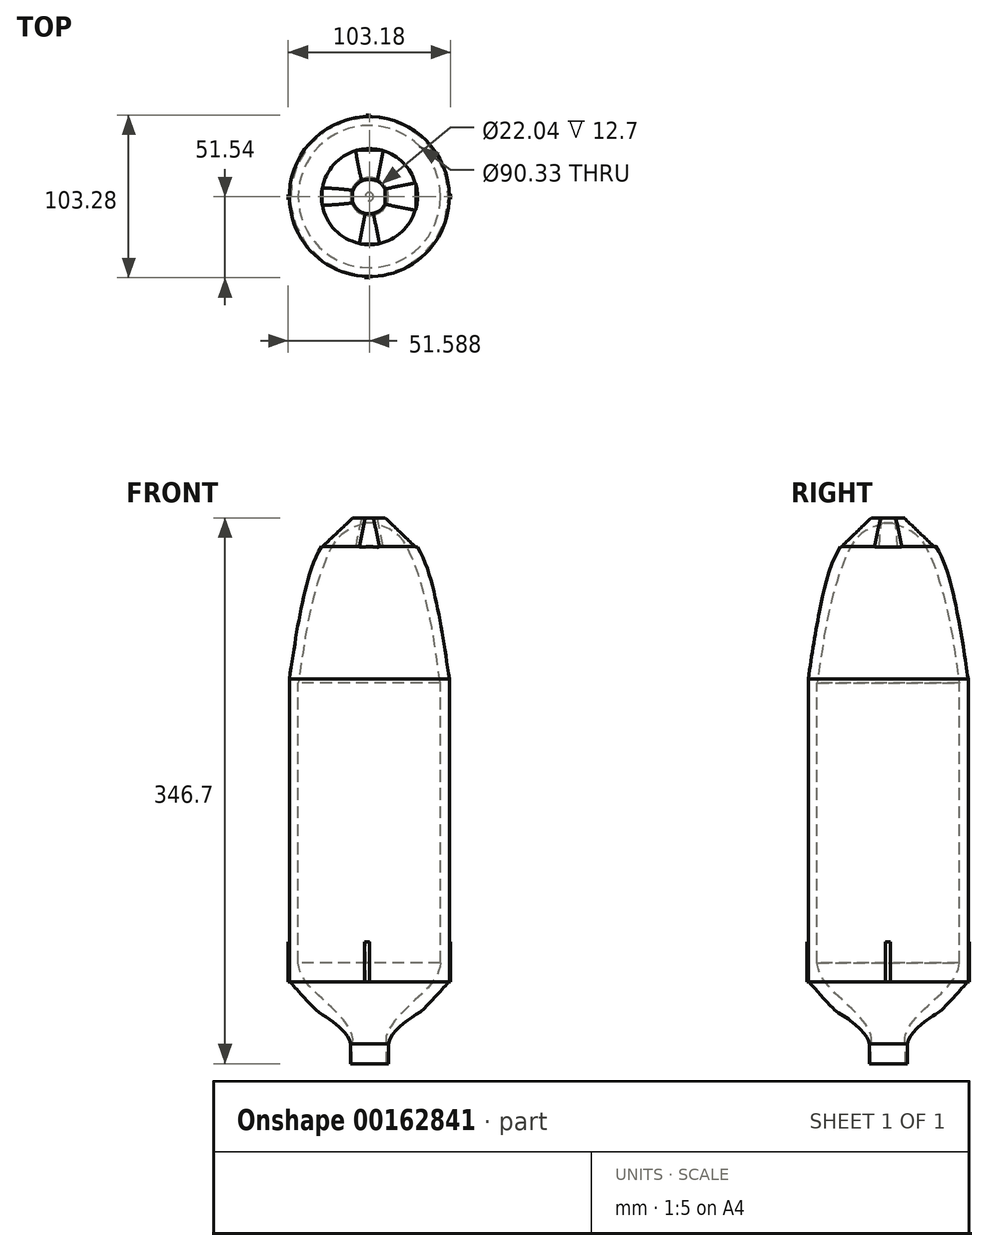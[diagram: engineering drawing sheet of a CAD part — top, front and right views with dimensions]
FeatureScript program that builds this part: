
annotation { "Feature Type Name" : "Feature", "Feature Type Description" : "" }
export const myFeature = defineFeature(function(context is Context, id is Id, definition is map)
    precondition{}
    {
        {
            var Q0;
            Q0=qCreatedBy(makeId("Front.planeOp"),FACE);
            var sketch = newSketch(context, id + "F0", { "sketchPlane" : qUnion([Q0])});
            skLineSegment(sketch, "E0", {"start": v(-60.21, 31.3) * mm, "end": v(-60.21, -146.5) * mm});
            skLineSegment(sketch, "E1", {"start": v(-9.41, 186.57) * mm, "end": v(-9.41, -181.27) * mm});
            skLineSegment(sketch, "E2", {"start": v(-60.21, 31.3) * mm, "end": v(-60.21, 133.73) * mm});
            skFitSpline(sketch, "E3", {"points": [v(-60.21, 31.3) * mm, v(-53.46, 72.41) * mm, v(-39.78, 115.49) * mm, v(-20.52, 133.73) * mm], "startDerivative": vector(16.73, 112.62) * mm, "endDerivative": vector(74.74, 52.6) * mm});
            skLineSegment(sketch, "E4", {"start": v(-20.52, 133.73) * mm, "end": v(-9.41, 133.73) * mm});
            skLineSegment(sketch, "E5", {"start": v(-21.48, -200.27) * mm, "end": v(-9.22, -200.27) * mm});
            skLineSegment(sketch, "E6", {"start": v(-54.58, 28.83) * mm, "end": v(-54.58, -148.97) * mm});
            skLineSegment(sketch, "E7", {"start": v(-3.78, 184.45) * mm, "end": v(-3.78, -183.39) * mm});
            skFitSpline(sketch, "E8", {"points": [v(-54.58, 28.83) * mm, v(-48.05, 69.53) * mm, v(-34.17, 113.63) * mm, v(-12.02, 130.37) * mm], "startDerivative": vector(18.83, 112.22) * mm, "endDerivative": vector(142.02, 42.2) * mm});
            skLineSegment(sketch, "E9", {"start": v(-12.02, 130.37) * mm, "end": v(-3.78, 130.37) * mm});
            skFitSpline(sketch, "E10", {"points": [v(-54.58, -148.97) * mm, v(-46.32, -164.98) * mm, v(-28.75, -182.02) * mm, v(-20.43, -200.27) * mm], "startDerivative": vector(6.77, -62.42) * mm, "endDerivative": vector(-19.43, -49.45) * mm});
            skLineSegment(sketch, "E11", {"start": v(-20.43, -200.27) * mm, "end": v(93.11, -200.27) * mm});
            skLineSegment(sketch, "E12", {"start": v(-60.21, -146.5) * mm, "end": v(-60.21, -161.1) * mm});
            skLineSegment(sketch, "E13", {"start": v(-60.21, -161.1) * mm, "end": v(-59.64, -161.1) * mm});
            skFitSpline(sketch, "E14", {"points": [v(-59.64, -161.1) * mm, v(-54.8, -166.59) * mm, v(-43.08, -179) * mm, v(-36.44, -183.52) * mm, v(-21.48, -200.27) * mm], "startDerivative": vector(23.82, -31.92) * mm, "endDerivative": vector(1.05, -49.25) * mm});
            skLineSegment(sketch, "E15", {"start": v(-39.78, 115.49) * mm, "end": v(-20.52, 133.73) * mm});
            skSolve(sketch);
        }
        {
            var Q0;
            Q0=makeQuery(id+"F0.imprint","IMPRINT",FACE,{"disambiguationData":[TD([[makeQuery(id+"F0.imprint","IMPRINT",EDGE,{"derivedFrom":sQuery(id+"F0.wireOp",EDGE,"E0")}),1.0]])]});
            var Q1;
            Q1=sQuery(id+"F0.wireOp",EDGE,"E1");
            revolve(context, id + "F1", {"entities" : qUnion([Q0]), "axis" : qUnion([Q1]), "revolveType" : RevolveType.FULL});
        }
        {
            var Q0;
            Q0=makeQuery(id+"F1.opRevolve","SWEPT_FACE",FACE,{"disambiguationData":[OSD([sQuery(id+"F0.wireOp",EDGE,"E13")])]});
            var sketch = newSketch(context, id + "F2", { "sketchPlane" : qUnion([Q0])});
            skLineSegment(sketch, "E16.bottom", {"start": v(-61, 2) * mm, "end": v(-60.2, 2) * mm});
            skLineSegment(sketch, "E16.top", {"start": v(-61, -1.35) * mm, "end": v(-60.2, -1.35) * mm});
            skLineSegment(sketch, "E16.left", {"start": v(-61, 2) * mm, "end": v(-61, -1.35) * mm});
            skLineSegment(sketch, "E16.right", {"start": v(-60.2, 2) * mm, "end": v(-60.2, -1.35) * mm});
            skLineSegment(sketch, "E17.bottom", {"start": v(-12.36, 50.8) * mm, "end": v(-9.4, 50.8) * mm});
            skLineSegment(sketch, "E17.top", {"start": v(-12.36, 50.23) * mm, "end": v(-9.4, 50.23) * mm});
            skLineSegment(sketch, "E17.left", {"start": v(-12.36, 50.8) * mm, "end": v(-12.36, 50.23) * mm});
            skLineSegment(sketch, "E17.right", {"start": v(-9.4, 50.8) * mm, "end": v(-9.4, 50.23) * mm});
            skLineSegment(sketch, "E18.bottom", {"start": v(42.18, 1.62) * mm, "end": v(40.8, 1.62) * mm});
            skLineSegment(sketch, "E18.top", {"start": v(42.18, -1.51) * mm, "end": v(40.8, -1.51) * mm});
            skLineSegment(sketch, "E18.left", {"start": v(42.18, 1.62) * mm, "end": v(42.18, -1.51) * mm});
            skLineSegment(sketch, "E18.right", {"start": v(40.8, 1.62) * mm, "end": v(40.8, -1.51) * mm});
            skLineSegment(sketch, "E19.bottom", {"start": v(-11.37, -50.2) * mm, "end": v(-8.54, -50.2) * mm});
            skLineSegment(sketch, "E19.top", {"start": v(-11.37, -51.74) * mm, "end": v(-8.54, -51.74) * mm});
            skLineSegment(sketch, "E19.left", {"start": v(-11.37, -50.2) * mm, "end": v(-11.37, -51.74) * mm});
            skLineSegment(sketch, "E19.right", {"start": v(-8.54, -50.2) * mm, "end": v(-8.54, -51.74) * mm});
            skLineSegment(sketch, "E20.bottom", {"start": v(-60.2, 2) * mm, "end": v(-59.62, 2) * mm});
            skLineSegment(sketch, "E20.top", {"start": v(-60.2, -1.36) * mm, "end": v(-59.62, -1.36) * mm});
            skLineSegment(sketch, "E20.left", {"start": v(-60.2, 2) * mm, "end": v(-60.2, -1.36) * mm});
            skLineSegment(sketch, "E20.right", {"start": v(-59.62, 2) * mm, "end": v(-59.62, -1.36) * mm});
            skLineSegment(sketch, "E21.bottom", {"start": v(-12.36, 50.8) * mm, "end": v(-9.39, 50.8) * mm});
            skLineSegment(sketch, "E21.top", {"start": v(-12.36, 51.54) * mm, "end": v(-9.39, 51.54) * mm});
            skLineSegment(sketch, "E21.left", {"start": v(-12.36, 50.8) * mm, "end": v(-12.36, 51.54) * mm});
            skLineSegment(sketch, "E21.right", {"start": v(-9.39, 50.8) * mm, "end": v(-9.39, 51.54) * mm});
            skSolve(sketch);
        }
        {
            var Q0;
            {var subQ1=sQuery(id+"F0.wireOp",EDGE,"E13");var subQ4=makeQuery(id+"F1.opRevolve","SWEPT_EDGE",EDGE,{"disambiguationData":[OSD([sQuery(id+"F0.wireOp",EDGE,"E12"),subQ1])]});var subQ6=sQuery(id+"F2.wireOp",EDGE,"E19.right");var subQ8=makeQuery(id+"F2.imprint","INTERSECT",VERTEX,{"derivedFrom":[subQ4,subQ6]});Q0=makeQuery(id+"F2.imprint","IMPRINT",FACE,{"disambiguationData":[TD([[makeQuery(id+"F2.imprint","IMPRINT",EDGE,{"disambiguationData":[TD([[subQ8,1.0]])],"derivedFrom":subQ6}),-1.0]])]});}
            var Q1;
            {var subQ0=sQuery(id+"F2.wireOp",EDGE,"E18.bottom");var subQ6=sQuery(id+"F2.wireOp",EDGE,"E18.right");var subQ10=makeQuery(id+"F2.imprint","INTERSECT",VERTEX,{"derivedFrom":[subQ0,subQ6]});Q1=makeQuery(id+"F2.imprint","IMPRINT",FACE,{"disambiguationData":[TD([[makeQuery(id+"F2.imprint","IMPRINT",EDGE,{"disambiguationData":[TD([[subQ10,1.0]])],"derivedFrom":subQ0}),1.0]])]});}
            var Q2;
            {var subQ0=sQuery(id+"F2.wireOp",EDGE,"E17.top");Q2=makeQuery(id+"F2.imprint","IMPRINT",FACE,{"disambiguationData":[TD([[makeQuery(id+"F2.imprint","IMPRINT",EDGE,{"derivedFrom":subQ0}),1.0]])]});}
            var Q3;
            {var subQ0=sQuery(id+"F2.wireOp",EDGE,"E20.right");var subQ1=sQuery(id+"F2.wireOp",EDGE,"E20.bottom");var subQ2=makeQuery(id+"F2.imprint","INTERSECT",VERTEX,{"derivedFrom":[subQ1,subQ0]});Q3=makeQuery(id+"F2.imprint","IMPRINT",FACE,{"disambiguationData":[TD([[makeQuery(id+"F2.imprint","IMPRINT",EDGE,{"disambiguationData":[TD([[subQ2,1.0]])],"derivedFrom":subQ1}),-1.0]])]});}
            var Q4;
            {var subQ1=sQuery(id+"F2.wireOp",EDGE,"E16.bottom");Q4=makeQuery(id+"F2.imprint","IMPRINT",FACE,{"disambiguationData":[TD([[makeQuery(id+"F2.imprint","IMPRINT",EDGE,{"derivedFrom":subQ1}),-1.0]])]});}
            var Q5;
            {var subQ0=sQuery(id+"F2.wireOp",EDGE,"E17.bottom");Q5=makeQuery(id+"F2.imprint","IMPRINT",FACE,{"disambiguationData":[TD([[makeQuery(id+"F2.imprint","IMPRINT",EDGE,{"derivedFrom":subQ0}),-1.0]])]});}
            var Q6;
            {var subQ0=sQuery(id+"F2.wireOp",EDGE,"E18.left");Q6=makeQuery(id+"F2.imprint","IMPRINT",FACE,{"disambiguationData":[TD([[makeQuery(id+"F2.imprint","IMPRINT",EDGE,{"derivedFrom":subQ0}),-1.0]])]});}
            var Q7;
            {var subQ0=sQuery(id+"F2.wireOp",EDGE,"E19.top");Q7=makeQuery(id+"F2.imprint","IMPRINT",FACE,{"disambiguationData":[TD([[makeQuery(id+"F2.imprint","IMPRINT",EDGE,{"derivedFrom":subQ0}),1.0]])]});}
            var Q8;
            Q8=makeQuery(id+"F2.imprint","IMPRINT",FACE,{"disambiguationData":[TD([[makeQuery(id+"F2.imprint","IMPRINT",EDGE,{"derivedFrom":sQuery(id+"F2.wireOp",EDGE,"E21.top")}),-1.0]])]});
            extrude(context, id + "F3", {"entities" : qUnion([Q0, Q1, Q2, Q3, Q4, Q5, Q6, Q7, Q8]), "operationType" : NewBodyOperationType.ADD, "oppositeDirection" : true, "depth" : 25.4 * mm});
        }
        {
            var Q0;
            Q0=makeQuery(id+"F3.opExtrude","SWEPT_FACE",FACE,{"disambiguationData":[OSD([sQuery(id+"F2.wireOp",EDGE,"E21.top")])]});
            var sketch = newSketch(context, id + "F4", { "sketchPlane" : qUnion([Q0])});
            skLineSegment(sketch, "E22", {"start": v(-19.97, 133.59) * mm, "end": v(-39.52, 115.25) * mm});
            skLineSegment(sketch, "E23", {"start": v(-39.52, 115.25) * mm, "end": v(-40.35, 116.13) * mm});
            skLineSegment(sketch, "E24", {"start": v(-40.35, 116.13) * mm, "end": v(-21.05, 134.18) * mm});
            skLineSegment(sketch, "E25", {"start": v(-21.05, 134.18) * mm, "end": v(-19.97, 133.59) * mm});
            skSolve(sketch);
        }
        {
            var Q0;
            Q0=makeQuery(id+"F4.imprint","IMPRINT",FACE,{"disambiguationData":[TD([[makeQuery(id+"F4.imprint","IMPRINT",EDGE,{"derivedFrom":sQuery(id+"F4.wireOp",EDGE,"E22")}),-1.0]])]});
            extrude(context, id + "F5", {"entities" : qUnion([Q0]), "operationType" : NewBodyOperationType.REMOVE, "oppositeDirection" : true, "depth" : 254 * mm});
        }
        {
            var Q0;
            Q0=makeQuery(id+"F3.opExtrude","SWEPT_FACE",FACE,{"disambiguationData":[OSD([sQuery(id+"F2.wireOp",EDGE,"E16.left")])]});
            var sketch = newSketch(context, id + "F6", { "sketchPlane" : qUnion([Q0])});
            skLineSegment(sketch, "E26", {"start": v(-29.48, 115.1) * mm, "end": v(-10.36, 133.36) * mm});
            skLineSegment(sketch, "E27", {"start": v(-10.36, 133.36) * mm, "end": v(-11.78, 134.84) * mm});
            skLineSegment(sketch, "E28", {"start": v(-11.78, 134.84) * mm, "end": v(-30.68, 116.8) * mm});
            skLineSegment(sketch, "E29", {"start": v(-30.68, 116.8) * mm, "end": v(-29.48, 115.1) * mm});
            skSolve(sketch);
        }
        {
            var Q0;
            Q0=makeQuery(id+"F6.imprint","IMPRINT",FACE,{"disambiguationData":[TD([[makeQuery(id+"F6.imprint","IMPRINT",EDGE,{"derivedFrom":sQuery(id+"F6.wireOp",EDGE,"E26")}),1.0]])]});
            extrude(context, id + "F7", {"entities" : qUnion([Q0]), "operationType" : NewBodyOperationType.REMOVE, "oppositeDirection" : true, "depth" : 254 * mm});
        }
        {
            var Q0;
            Q0=makeQuery(id+"F3.opExtrude","SWEPT_FACE",FACE,{"disambiguationData":[OSD([sQuery(id+"F2.wireOp",EDGE,"E19.top")])]});
            var sketch = newSketch(context, id + "F8", { "sketchPlane" : qUnion([Q0])});
            skLineSegment(sketch, "E30", {"start": v(-20.14, 115.05) * mm, "end": v(0, 134.34) * mm});
            skLineSegment(sketch, "E31", {"start": v(0, 134.34) * mm, "end": v(-2.22, 134.34) * mm});
            skLineSegment(sketch, "E32", {"start": v(-2.22, 134.34) * mm, "end": v(-22.19, 115.22) * mm});
            skLineSegment(sketch, "E33", {"start": v(-22.19, 115.22) * mm, "end": v(-20.14, 115.05) * mm});
            skSolve(sketch);
        }
        {
            var Q0;
            Q0=makeQuery(id+"F8.imprint","IMPRINT",FACE,{"disambiguationData":[TD([[makeQuery(id+"F8.imprint","IMPRINT",EDGE,{"derivedFrom":sQuery(id+"F8.wireOp",EDGE,"E30")}),1.0]])]});
            extrude(context, id + "F9", {"entities" : qUnion([Q0]), "operationType" : NewBodyOperationType.REMOVE, "oppositeDirection" : true, "depth" : 254 * mm});
        }
        {
            var Q0;
            Q0=makeQuery(id+"F3.opExtrude","SWEPT_FACE",FACE,{"disambiguationData":[OSD([sQuery(id+"F2.wireOp",EDGE,"E18.left")])]});
            var sketch = newSketch(context, id + "F10", { "sketchPlane" : qUnion([Q0])});
            skLineSegment(sketch, "E34", {"start": v(-30.2, 114.99) * mm, "end": v(-9.95, 134.55) * mm});
            skLineSegment(sketch, "E35", {"start": v(-11.75, 134.55) * mm, "end": v(-30.74, 116.22) * mm});
            skLineSegment(sketch, "E36", {"start": v(-30.74, 116.22) * mm, "end": v(-30.2, 114.99) * mm});
            skLineSegment(sketch, "E37", {"start": v(-9.95, 134.55) * mm, "end": v(-11.75, 134.55) * mm});
            skSolve(sketch);
        }
        {
            var Q0;
            Q0=makeQuery(id+"F10.imprint","IMPRINT",FACE,{"disambiguationData":[TD([[makeQuery(id+"F10.imprint","IMPRINT",EDGE,{"derivedFrom":sQuery(id+"F10.wireOp",EDGE,"E34")}),1.0]])]});
            extrude(context, id + "F11", {"entities" : qUnion([Q0]), "operationType" : NewBodyOperationType.REMOVE, "oppositeDirection" : true, "depth" : 254 * mm});
        }
        {
            var Q0;
            Q0=makeQuery(id+"F1.opRevolve","SWEPT_FACE",FACE,{"disambiguationData":[OSD([sQuery(id+"F0.wireOp",EDGE,"E5")])]});
            extrude(context, id + "F12", {"entities" : qUnion([Q0]), "operationType" : NewBodyOperationType.ADD, "depth" : 12.7 * mm});
        }
    });
